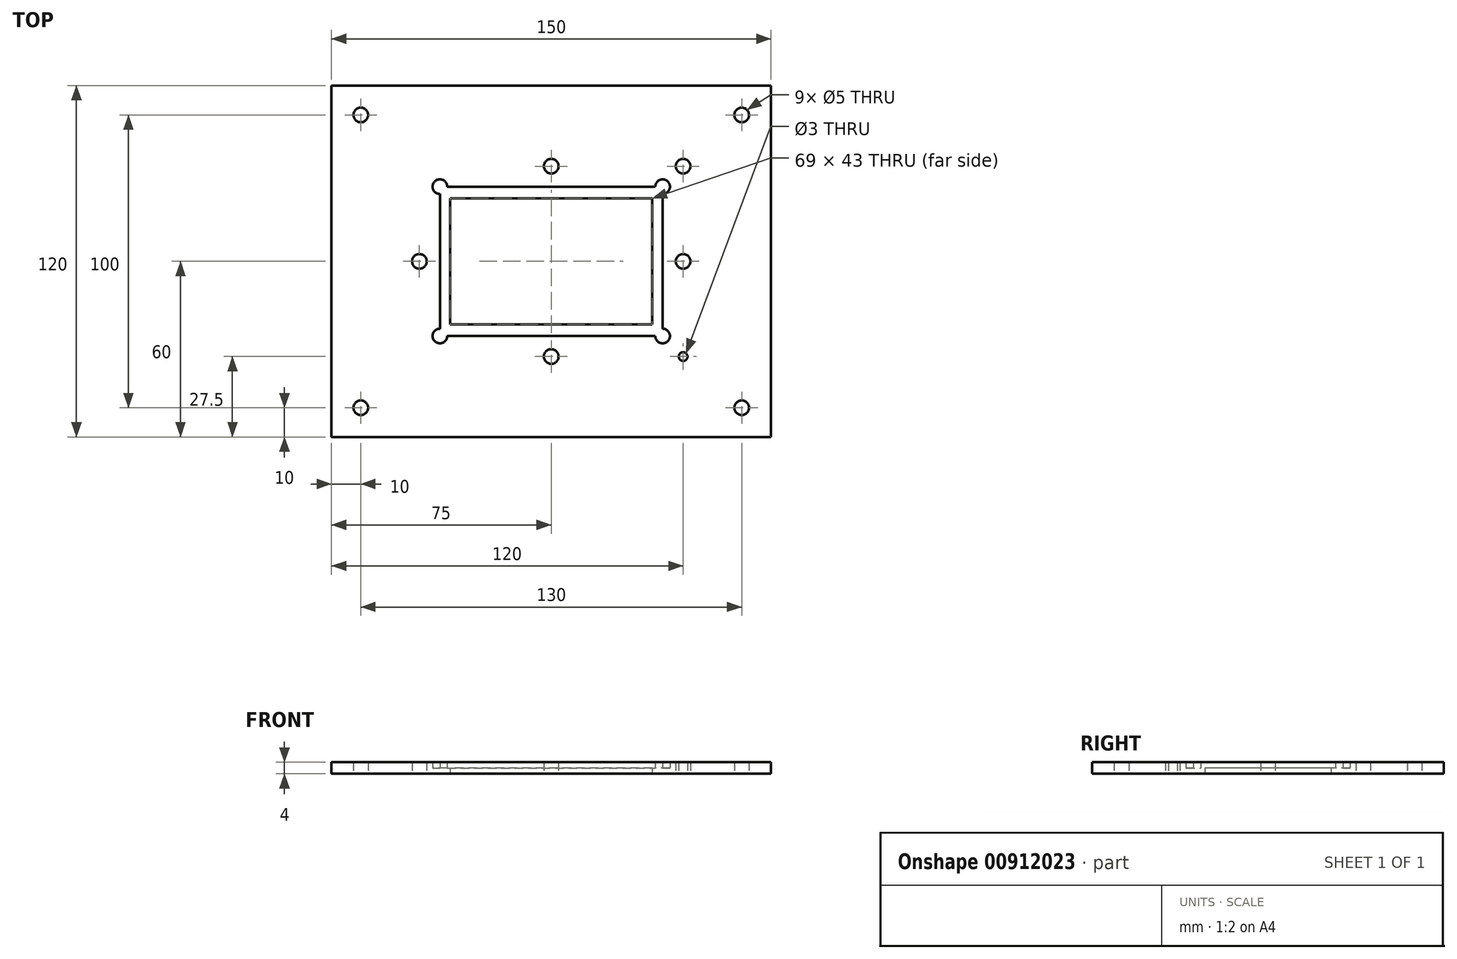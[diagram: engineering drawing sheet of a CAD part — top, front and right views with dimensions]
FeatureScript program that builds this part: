
annotation { "Feature Type Name" : "Feature", "Feature Type Description" : "" }
export const myFeature = defineFeature(function(context is Context, id is Id, definition is map)
    precondition{}
    {
        {
            var Q0;
            Q0=qCreatedBy(makeId("Top.planeOp"),FACE);
            var sketch = newSketch(context, id + "F0", { "sketchPlane" : qUnion([Q0])});
            skLineSegment(sketch, "E0.bottom", {"start": v(37.5, 25) * mm, "end": v(-37.5, 25) * mm, "construction": true});
            skLineSegment(sketch, "E0.top", {"start": v(37.5, -25) * mm, "end": v(-37.5, -25) * mm, "construction": true});
            skLineSegment(sketch, "E0.left", {"start": v(37.5, 25) * mm, "end": v(37.5, -25) * mm, "construction": true});
            skLineSegment(sketch, "E0.right", {"start": v(-37.5, 25) * mm, "end": v(-37.5, -25) * mm, "construction": true});
            skPoint(sketch, "E0.middle", {"position": v(0, 0) * mm});
            skLineSegment(sketch, "E1.bottom", {"start": v(34.5, 21.5) * mm, "end": v(-34.5, 21.5) * mm});
            skLineSegment(sketch, "E1.top", {"start": v(34.5, -21.5) * mm, "end": v(-34.5, -21.5) * mm});
            skLineSegment(sketch, "E1.left", {"start": v(34.5, 21.5) * mm, "end": v(34.5, -21.5) * mm});
            skLineSegment(sketch, "E1.right", {"start": v(-34.5, 21.5) * mm, "end": v(-34.5, -21.5) * mm});
            skLineSegment(sketch, "E2.bottom", {"start": v(-38, 25.5) * mm, "end": v(38, 25.5) * mm, "construction": true});
            skLineSegment(sketch, "E2.top", {"start": v(-38, -25.5) * mm, "end": v(38, -25.5) * mm, "construction": true});
            skLineSegment(sketch, "E2.left", {"start": v(-38, 25.5) * mm, "end": v(-38, -25.5) * mm, "construction": true});
            skLineSegment(sketch, "E2.right", {"start": v(38, 25.5) * mm, "end": v(38, -25.5) * mm, "construction": true});
            skLineSegment(sketch, "E3.bottom", {"start": v(75, 60) * mm, "end": v(-75, 60) * mm});
            skLineSegment(sketch, "E3.top", {"start": v(75, -60) * mm, "end": v(-75, -60) * mm});
            skLineSegment(sketch, "E3.left", {"start": v(75, 60) * mm, "end": v(75, -60) * mm});
            skLineSegment(sketch, "E3.right", {"start": v(-75, 60) * mm, "end": v(-75, -60) * mm});
            skCircle(sketch, "E4", {"center": v(38, 25.5) * mm, "radius": 2.5 * mm, "construction": true});
            skCircle(sketch, "E5", {"center": v(-38, 25.5) * mm, "radius": 2.5 * mm, "construction": true});
            skCircle(sketch, "E6", {"center": v(-38, -25.5) * mm, "radius": 2.5 * mm, "construction": true});
            skCircle(sketch, "E7", {"center": v(38, -25.5) * mm, "radius": 2.5 * mm, "construction": true});
            skPoint(sketch, "E8", {"position": v(-38, -23) * mm});
            skPoint(sketch, "E9", {"position": v(-35.5, -25.5) * mm});
            skPoint(sketch, "E10", {"position": v(-35.5, 25.5) * mm});
            skPoint(sketch, "E11", {"position": v(-38, 23) * mm});
            skPoint(sketch, "E12", {"position": v(38, 23) * mm});
            skPoint(sketch, "E13", {"position": v(35.5, 25.5) * mm});
            skPoint(sketch, "E14", {"position": v(38, -23) * mm});
            skPoint(sketch, "E15", {"position": v(35.5, -25.5) * mm});
            skArc(sketch, "E16", {"start": v(35.5, 25.5) * mm, "mid": v(39.77, 27.27) * mm, "end": v(38, 23) * mm});
            skArc(sketch, "E17", {"start": v(38, -23) * mm, "mid": v(39.77, -27.27) * mm, "end": v(35.5, -25.5) * mm});
            skArc(sketch, "E18", {"start": v(-35.5, -25.5) * mm, "mid": v(-39.77, -27.27) * mm, "end": v(-38, -23) * mm});
            skArc(sketch, "E19", {"start": v(-35.5, 25.5) * mm, "mid": v(-39.77, 27.27) * mm, "end": v(-38, 23) * mm});
            skLineSegment(sketch, "E20", {"start": v(-35.5, 25.5) * mm, "end": v(35.5, 25.5) * mm});
            skLineSegment(sketch, "E21", {"start": v(-38, 23) * mm, "end": v(-38, -23) * mm});
            skLineSegment(sketch, "E22", {"start": v(-35.5, -25.5) * mm, "end": v(35.5, -25.5) * mm});
            skLineSegment(sketch, "E23", {"start": v(38, -23) * mm, "end": v(38, 23) * mm});
            skLineSegment(sketch, "E24.bottom", {"start": v(-45, 32.5) * mm, "end": v(45, 32.5) * mm, "construction": true});
            skLineSegment(sketch, "E24.top", {"start": v(-45, -32.5) * mm, "end": v(45, -32.5) * mm, "construction": true});
            skLineSegment(sketch, "E24.left", {"start": v(-45, 32.5) * mm, "end": v(-45, -32.5) * mm, "construction": true});
            skLineSegment(sketch, "E24.right", {"start": v(45, 32.5) * mm, "end": v(45, -32.5) * mm, "construction": true});
            skLineSegment(sketch, "E25", {"start": v(0, 0) * mm, "end": v(0, 32.5) * mm, "construction": true});
            skLineSegment(sketch, "E26", {"start": v(0, 0) * mm, "end": v(0, -32.5) * mm, "construction": true});
            skLineSegment(sketch, "E27", {"start": v(0, 0) * mm, "end": v(45, 0) * mm, "construction": true});
            skLineSegment(sketch, "E28", {"start": v(0, 0) * mm, "end": v(-45, 0) * mm, "construction": true});
            skCircle(sketch, "E29", {"center": v(0, 32.5) * mm, "radius": 2.5 * mm});
            skCircle(sketch, "E30", {"center": v(-45, 0) * mm, "radius": 2.5 * mm});
            skCircle(sketch, "E31", {"center": v(0, -32.5) * mm, "radius": 2.5 * mm});
            skCircle(sketch, "E32", {"center": v(45, 0) * mm, "radius": 2.5 * mm});
            skCircle(sketch, "E33", {"center": v(45, 32.5) * mm, "radius": 2.5 * mm});
            skCircle(sketch, "E34", {"center": v(45, -32.5) * mm, "radius": 1.5 * mm});
            skPoint(sketch, "E35", {"position": v(-65, 50) * mm});
            skPoint(sketch, "E36", {"position": v(65, 50) * mm});
            skPoint(sketch, "E37", {"position": v(-65, -50) * mm});
            skPoint(sketch, "E38", {"position": v(65, -50) * mm});
            skCircle(sketch, "E39", {"center": v(-65, 50) * mm, "radius": 2.5 * mm});
            skCircle(sketch, "E40", {"center": v(-65, -50) * mm, "radius": 2.5 * mm});
            skCircle(sketch, "E41", {"center": v(65, -50) * mm, "radius": 2.5 * mm});
            skCircle(sketch, "E42", {"center": v(65, 50) * mm, "radius": 2.5 * mm});
            skSolve(sketch);
        }
        {
            var Q0;
            Q0=makeQuery(id+"F0.imprint","IMPRINT",FACE,{"disambiguationData":[TD([[makeQuery(id+"F0.imprint","IMPRINT",EDGE,{"derivedFrom":sQuery(id+"F0.wireOp",EDGE,"E3.bottom")}),1.0]])]});
            extrude(context, id + "F1", {"entities" : qUnion([Q0]), "depth" : 4 * mm, "offsetDistance" : 25 * mm});
        }
        {
            var Q0;
            Q0=makeQuery(id+"F0.imprint","IMPRINT",FACE,{"disambiguationData":[TD([[makeQuery(id+"F0.imprint","IMPRINT",EDGE,{"derivedFrom":sQuery(id+"F0.wireOp",EDGE,"E1.bottom")}),-1.0]])]});
            extrude(context, id + "F2", {"entities" : qUnion([Q0]), "operationType" : NewBodyOperationType.ADD, "depth" : 2 * mm, "offsetDistance" : 25 * mm});
        }
    });
